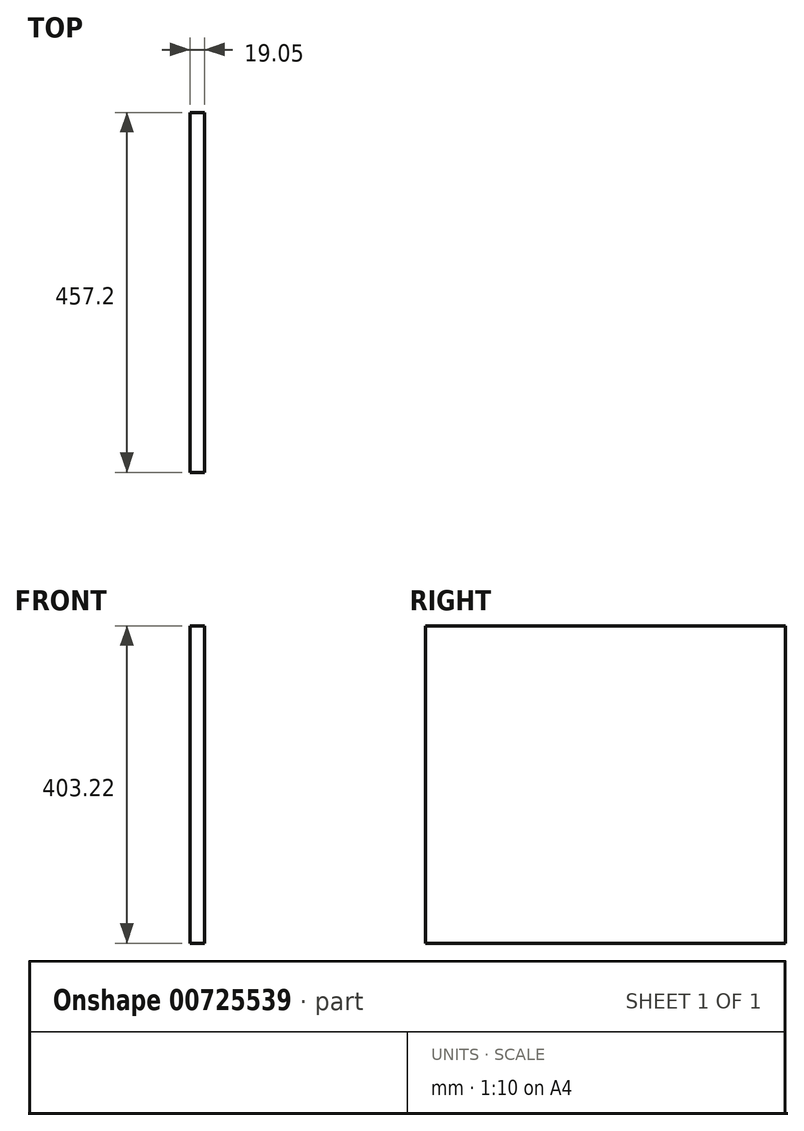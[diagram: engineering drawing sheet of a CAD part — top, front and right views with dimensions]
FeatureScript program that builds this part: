
annotation { "Feature Type Name" : "Feature", "Feature Type Description" : "" }
export const myFeature = defineFeature(function(context is Context, id is Id, definition is map)
    precondition{}
    {
        {
            var Q0;
            Q0=qCreatedBy(makeId("Right.planeOp"),FACE);
            var sketch = newSketch(context, id + "F0", { "sketchPlane" : qUnion([Q0])});
            skLineSegment(sketch, "E0.bottom", {"start": v(228.6, 201.61) * mm, "end": v(-228.6, 201.61) * mm});
            skLineSegment(sketch, "E0.top", {"start": v(228.6, -201.61) * mm, "end": v(-228.6, -201.61) * mm});
            skLineSegment(sketch, "E0.left", {"start": v(228.6, 201.61) * mm, "end": v(228.6, -201.61) * mm});
            skLineSegment(sketch, "E0.right", {"start": v(-228.6, 201.61) * mm, "end": v(-228.6, -201.61) * mm});
            skPoint(sketch, "E0.middle", {"position": v(0, 0) * mm});
            skSolve(sketch);
        }
        {
            var Q0;
            Q0=makeQuery(id+"F0.imprint","IMPRINT",FACE,{"disambiguationData":[TD([[makeQuery(id+"F0.imprint","IMPRINT",EDGE,{"derivedFrom":sQuery(id+"F0.wireOp",EDGE,"E0.bottom")}),1.0]])]});
            extrude(context, id + "F1", {"entities" : qUnion([Q0]), "depth" : 19.05 * mm, "offsetDistance" : 25.4 * mm});
        }
    });
